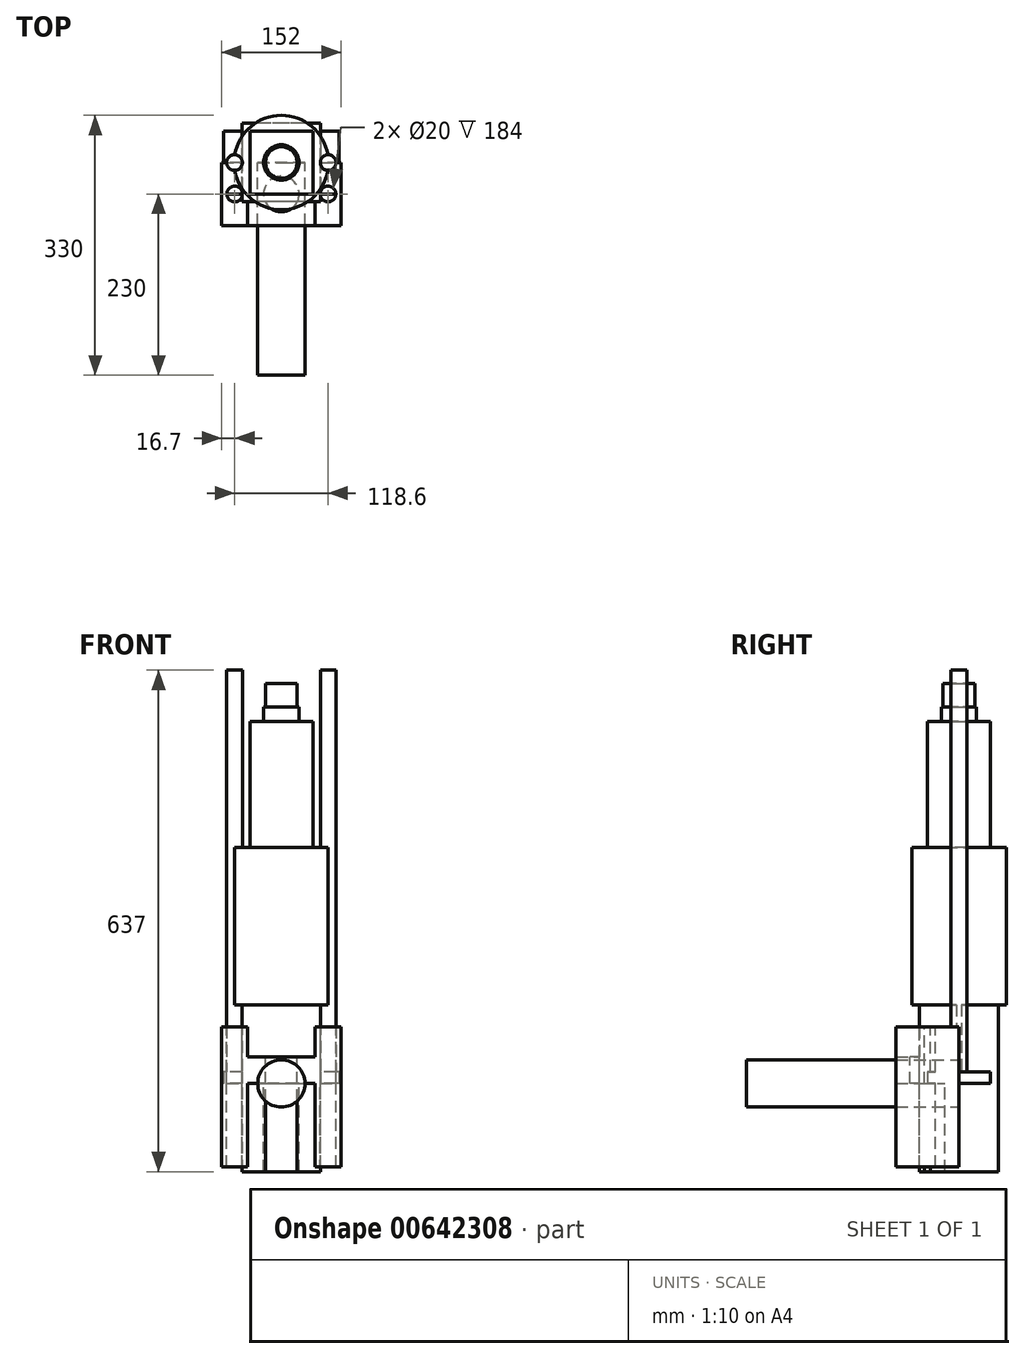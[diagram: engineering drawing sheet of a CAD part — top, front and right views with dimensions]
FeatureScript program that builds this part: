
annotation { "Feature Type Name" : "Feature", "Feature Type Description" : "" }
export const myFeature = defineFeature(function(context is Context, id is Id, definition is map)
    precondition{}
    {
        {
            var Q0;
            Q0=qCreatedBy(makeId("Top.planeOp"),FACE);
            var sketch = newSketch(context, id + "F0", { "sketchPlane" : qUnion([Q0])});
            skLineSegment(sketch, "E0.bottom", {"start": v(40, -40) * mm, "end": v(-40, -40) * mm});
            skLineSegment(sketch, "E0.top", {"start": v(40, 40) * mm, "end": v(-40, 40) * mm});
            skLineSegment(sketch, "E0.left", {"start": v(40, -40) * mm, "end": v(40, 40) * mm});
            skLineSegment(sketch, "E0.right", {"start": v(-40, -40) * mm, "end": v(-40, 40) * mm});
            skPoint(sketch, "E0.middle", {"position": v(0, 0) * mm});
            skSolve(sketch);
        }
        {
            var Q0;
            Q0=makeQuery(id+"F0.imprint","IMPRINT",FACE,{"disambiguationData":[TD([[makeQuery(id+"F0.imprint","IMPRINT",EDGE,{"derivedFrom":sQuery(id+"F0.wireOp",EDGE,"E0.bottom")}),-1.0]])]});
            extrude(context, id + "F1", {"entities" : qUnion([Q0]), "depth" : (620 - 112 - 48) * mm, "offsetDistance" : 25 * mm});
        }
        {
            var Q0;
            Q0=makeQuery(id+"F1.opExtrude","CAP_FACE",FACE,{"disambiguationData":[OSD([sQuery(id+"F0.wireOp",EDGE,"E0.bottom"),sQuery(id+"F0.wireOp",EDGE,"E0.top"),sQuery(id+"F0.wireOp",EDGE,"E0.left"),sQuery(id+"F0.wireOp",EDGE,"E0.right")])],"isStart":true});
            var sketch = newSketch(context, id + "F2", { "sketchPlane" : qUnion([Q0])});
            skLineSegment(sketch, "E1.bottom", {"start": v(50, -50) * mm, "end": v(-50, -50) * mm});
            skLineSegment(sketch, "E1.top", {"start": v(50, 50) * mm, "end": v(-50, 50) * mm});
            skLineSegment(sketch, "E1.left", {"start": v(50, -50) * mm, "end": v(50, 50) * mm});
            skLineSegment(sketch, "E1.right", {"start": v(-50, -50) * mm, "end": v(-50, 50) * mm});
            skPoint(sketch, "E1.middle", {"position": v(0, 0) * mm});
            skSolve(sketch);
        }
        {
            var Q0;
            Q0=makeQuery(id+"F2.imprint","IMPRINT",FACE,{"disambiguationData":[TD([[makeQuery(id+"F2.imprint","IMPRINT",EDGE,{"derivedFrom":makeQuery(id+"F1.opExtrude","CAP_EDGE",EDGE,{"disambiguationData":[OSD([sQuery(id+"F0.wireOp",EDGE,"E0.bottom")])],"isStart":true})}),1.0]])]});
            var Q1;
            Q1=makeQuery(id+"F2.imprint","IMPRINT",FACE,{"disambiguationData":[TD([[makeQuery(id+"F2.imprint","IMPRINT",EDGE,{"derivedFrom":sQuery(id+"F2.wireOp",EDGE,"E1.bottom")}),-1.0]])]});
            extrude(context, id + "F3", {"entities" : qUnion([Q0, Q1]), "operationType" : NewBodyOperationType.ADD, "depth" : 112 * mm, "offsetDistance" : 25 * mm});
        }
        {
            var Q0;
            Q0=makeQuery(id+"F1.opExtrude","CAP_FACE",FACE,{"disambiguationData":[OSD([sQuery(id+"F0.wireOp",EDGE,"E0.bottom"),sQuery(id+"F0.wireOp",EDGE,"E0.top"),sQuery(id+"F0.wireOp",EDGE,"E0.left"),sQuery(id+"F0.wireOp",EDGE,"E0.right")])],"isStart":false});
            var sketch = newSketch(context, id + "F4", { "sketchPlane" : qUnion([Q0])});
            skCircle(sketch, "E2", {"center": v(0, 0) * mm, "radius": 22.5 * mm});
            skCircle(sketch, "E3", {"center": v(0, 0) * mm, "radius": 20 * mm});
            skSolve(sketch);
        }
        {
            var Q0;
            Q0=makeQuery(id+"F4.imprint","IMPRINT",FACE,{"disambiguationData":[TD([[makeQuery(id+"F4.imprint","IMPRINT",EDGE,{"derivedFrom":sQuery(id+"F4.wireOp",EDGE,"E2")}),1.0]])]});
            extrude(context, id + "F5", {"entities" : qUnion([Q0]), "operationType" : NewBodyOperationType.ADD, "depth" : 18.5 * mm, "offsetDistance" : 25 * mm});
        }
        {
            var Q0;
            Q0=makeQuery(id+"F5.boolean.opBoolean","SPLIT",FACE,{"disambiguationData":[TD([makeQuery(id+"F5.opExtrude","SWEPT_FACE",FACE,{"disambiguationData":[OSD([sQuery(id+"F4.wireOp",EDGE,"E3")])]})])],"derivedFrom":makeQuery(id+"F1.opExtrude","CAP_FACE",FACE,{"disambiguationData":[OSD([sQuery(id+"F0.wireOp",EDGE,"E0.bottom"),sQuery(id+"F0.wireOp",EDGE,"E0.top"),sQuery(id+"F0.wireOp",EDGE,"E0.left"),sQuery(id+"F0.wireOp",EDGE,"E0.right")])],"isStart":false})});
            extrude(context, id + "F6", {"entities" : qUnion([Q0]), "operationType" : NewBodyOperationType.ADD, "depth" : 48 * mm, "offsetDistance" : 25 * mm});
        }
        {
            var Q0;
            Q0=qCreatedBy(makeId("Top.planeOp"),FACE);
            var sketch = newSketch(context, id + "F7", { "sketchPlane" : qUnion([Q0])});
            skCircle(sketch, "E4", {"center": v(0, 0) * mm, "radius": 20 * mm});
            skSolve(sketch);
        }
        {
            var Q0;
            Q0=makeQuery(id+"F7.imprint","IMPRINT",FACE,{"disambiguationData":[TD([[makeQuery(id+"F7.imprint","IMPRINT",EDGE,{"derivedFrom":sQuery(id+"F7.wireOp",EDGE,"E4")}),1.0]])]});
            extrude(context, id + "F8", {"entities" : qUnion([Q0]), "depth" : 400 * mm, "offsetDistance" : 25 * mm});
        }
        {
            var Q0;
            Q0=qCreatedBy(makeId("Front.planeOp"),FACE);
            var sketch = newSketch(context, id + "F9", { "sketchPlane" : qUnion([Q0])});
            skLineSegment(sketch, "E5", {"start": v(0, 0) * mm, "end": v(42.6, 0) * mm});
            skLineSegment(sketch, "E6", {"start": v(42.6, 0) * mm, "end": v(42.6, -106) * mm});
            skLineSegment(sketch, "E7", {"start": v(42.6, -106) * mm, "end": v(76, -106) * mm});
            skLineSegment(sketch, "E8", {"start": v(76, -106) * mm, "end": v(76, 72) * mm});
            skLineSegment(sketch, "E9", {"start": v(76, 72) * mm, "end": v(42.6, 72) * mm});
            skLineSegment(sketch, "E10", {"start": v(42.6, 72) * mm, "end": v(42.6, 34) * mm});
            skLineSegment(sketch, "E11", {"start": v(42.6, 34) * mm, "end": v(-42.6, 34) * mm});
            skLineSegment(sketch, "E12", {"start": v(-42.6, 34) * mm, "end": v(-42.6, 72) * mm});
            skLineSegment(sketch, "E13", {"start": v(-42.6, 72) * mm, "end": v(-76, 72) * mm});
            skLineSegment(sketch, "E14", {"start": v(-76, 72) * mm, "end": v(-76, -106) * mm});
            skLineSegment(sketch, "E15", {"start": v(-76, -106) * mm, "end": v(-42.6, -106) * mm});
            skLineSegment(sketch, "E16", {"start": v(-42.6, -106) * mm, "end": v(-42.6, 0) * mm});
            skLineSegment(sketch, "E17", {"start": v(-42.6, 0) * mm, "end": v(0, 0) * mm});
            skSolve(sketch);
        }
        {
            var Q0;
            Q0=makeQuery(id+"F9.imprint","IMPRINT",FACE,{"disambiguationData":[TD([[makeQuery(id+"F9.imprint","IMPRINT",EDGE,{"derivedFrom":sQuery(id+"F9.wireOp",EDGE,"E5")}),1.0]])]});
            extrude(context, id + "F10", {"entities" : qUnion([Q0]), "depth" : 80 * mm, "offsetDistance" : 25 * mm});
        }
        {
            var Q0;
            Q0=makeQuery(id+"F10.opExtrude","SWEPT_FACE",FACE,{"disambiguationData":[OSD([sQuery(id+"F9.wireOp",EDGE,"E13")])]});
            var sketch = newSketch(context, id + "F11", { "sketchPlane" : qUnion([Q0])});
            skCircle(sketch, "E18", {"center": v(-59.3, -40) * mm, "radius": 10 * mm});
            skPoint(sketch, "E18.centerSnap0", {"position": v(-59.3, -80) * mm});
            skSolve(sketch);
        }
        {
            var Q0;
            Q0=makeQuery(id+"F11.imprint","IMPRINT",FACE,{"disambiguationData":[TD([[makeQuery(id+"F11.imprint","IMPRINT",EDGE,{"derivedFrom":sQuery(id+"F11.wireOp",EDGE,"E18")}),1.0]])]});
            extrude(context, id + "F12", {"entities" : qUnion([Q0]), "operationType" : NewBodyOperationType.REMOVE, "endBound" : BoundingType.THROUGH_ALL, "oppositeDirection" : true, "depth" : 25 * mm, "offsetDistance" : 25 * mm});
        }
        {
            var Q0;
            Q0=makeQuery(id+"F10.opExtrude","SWEPT_FACE",FACE,{"disambiguationData":[OSD([sQuery(id+"F9.wireOp",EDGE,"E9")])]});
            var sketch = newSketch(context, id + "F13", { "sketchPlane" : qUnion([Q0])});
            skCircle(sketch, "E19", {"center": v(59.3, -40) * mm, "radius": 10 * mm});
            skPoint(sketch, "E19.centerSnap0", {"position": v(76, -40) * mm});
            skPoint(sketch, "E19.centerSnap1", {"position": v(59.3, -80) * mm});
            skSolve(sketch);
        }
        {
            var Q0;
            Q0=makeQuery(id+"F13.imprint","IMPRINT",FACE,{"disambiguationData":[TD([[makeQuery(id+"F13.imprint","IMPRINT",EDGE,{"derivedFrom":sQuery(id+"F13.wireOp",EDGE,"E19")}),1.0]])]});
            extrude(context, id + "F14", {"entities" : qUnion([Q0]), "operationType" : NewBodyOperationType.REMOVE, "endBound" : BoundingType.THROUGH_ALL, "oppositeDirection" : true, "depth" : 25 * mm, "offsetDistance" : 25 * mm});
        }
        {
            var Q0;
            Q0=makeQuery(id+"F10.opExtrude","SWEPT_FACE",FACE,{"disambiguationData":[OSD([sQuery(id+"F9.wireOp",EDGE,"E11")])]});
            var sketch = newSketch(context, id + "F15", { "sketchPlane" : qUnion([Q0])});
            skCircle(sketch, "E20", {"center": v(0, -40) * mm, "radius": 22.5 * mm});
            skPoint(sketch, "E20.centerSnap0", {"position": v(42.6, -40) * mm});
            skSolve(sketch);
        }
        {
            var Q0;
            Q0=makeQuery(id+"F15.imprint","IMPRINT",FACE,{"disambiguationData":[TD([[makeQuery(id+"F15.imprint","IMPRINT",EDGE,{"derivedFrom":sQuery(id+"F15.wireOp",EDGE,"E20")}),1.0]])]});
            extrude(context, id + "F16", {"entities" : qUnion([Q0]), "operationType" : NewBodyOperationType.REMOVE, "endBound" : BoundingType.THROUGH_ALL, "oppositeDirection" : true, "depth" : 25 * mm, "offsetDistance" : 25 * mm});
        }
        {
            var Q0;
            Q0=qCreatedBy(makeId("Top.planeOp"),FACE);
            var sketch = newSketch(context, id + "F17", { "sketchPlane" : qUnion([Q0])});
            skLineSegment(sketch, "E21.bottom", {"start": v(73.5, -40) * mm, "end": v(-73.5, -40) * mm});
            skLineSegment(sketch, "E21.top", {"start": v(73.5, 40) * mm, "end": v(-73.5, 40) * mm});
            skLineSegment(sketch, "E21.left", {"start": v(73.5, -40) * mm, "end": v(73.5, 40) * mm});
            skLineSegment(sketch, "E21.right", {"start": v(-73.5, -40) * mm, "end": v(-73.5, 40) * mm});
            skPoint(sketch, "E21.middle", {"position": v(0, 0) * mm});
            skSolve(sketch);
        }
        {
            var Q0;
            Q0=makeQuery(id+"F17.imprint","IMPRINT",FACE,{"disambiguationData":[TD([[makeQuery(id+"F17.imprint","IMPRINT",EDGE,{"derivedFrom":sQuery(id+"F17.wireOp",EDGE,"E21.bottom")}),-1.0]])]});
            extrude(context, id + "F18", {"entities" : qUnion([Q0]), "depth" : 15 * mm, "offsetDistance" : 25 * mm});
        }
        {
            var Q0;
            Q0=makeQuery(id+"F18.opExtrude","CAP_FACE",FACE,{"disambiguationData":[OSD([sQuery(id+"F17.wireOp",EDGE,"E21.bottom"),sQuery(id+"F17.wireOp",EDGE,"E21.top"),sQuery(id+"F17.wireOp",EDGE,"E21.left"),sQuery(id+"F17.wireOp",EDGE,"E21.right")])],"isStart":false});
            var sketch = newSketch(context, id + "F19", { "sketchPlane" : qUnion([Q0])});
            skCircle(sketch, "E22", {"center": v(-59.5, 0) * mm, "radius": 10 * mm});
            skCircle(sketch, "E23", {"center": v(59.5, 0) * mm, "radius": 10 * mm});
            skLineSegment(sketch, "E24", {"start": v(-73.5, 0) * mm, "end": v(-59.5, 0) * mm, "construction": true});
            skLineSegment(sketch, "E25", {"start": v(59.5, 0) * mm, "end": v(73.5, 0) * mm, "construction": true});
            skSolve(sketch);
        }
        {
            var Q0;
            Q0=makeQuery(id+"F19.imprint","IMPRINT",FACE,{"disambiguationData":[TD([[makeQuery(id+"F19.imprint","IMPRINT",EDGE,{"derivedFrom":sQuery(id+"F19.wireOp",EDGE,"E22")}),1.0]])]});
            var Q1;
            Q1=makeQuery(id+"F19.imprint","IMPRINT",FACE,{"disambiguationData":[TD([[makeQuery(id+"F19.imprint","IMPRINT",EDGE,{"derivedFrom":sQuery(id+"F19.wireOp",EDGE,"E23")}),1.0]])]});
            extrude(context, id + "F20", {"entities" : qUnion([Q0, Q1]), "operationType" : NewBodyOperationType.ADD, "depth" : (225 - 15 + 300) * mm, "offsetDistance" : 25 * mm});
        }
        {
            var Q0;
            Q0=qCreatedBy(makeId("Top.planeOp"),FACE);
            var sketch = newSketch(context, id + "F21", { "sketchPlane" : qUnion([Q0])});
            skLineSegment(sketch, "E26.bottom", {"start": v(50, -50) * mm, "end": v(-50, -50) * mm});
            skLineSegment(sketch, "E26.top", {"start": v(50, 50) * mm, "end": v(-50, 50) * mm});
            skLineSegment(sketch, "E26.left", {"start": v(50, -50) * mm, "end": v(50, 50) * mm});
            skLineSegment(sketch, "E26.right", {"start": v(-50, -50) * mm, "end": v(-50, 50) * mm});
            skPoint(sketch, "E26.middle", {"position": v(0, 0) * mm});
            skSolve(sketch);
        }
        {
            var Q0;
            Q0=makeQuery(id+"F21.imprint","IMPRINT",FACE,{"disambiguationData":[TD([[makeQuery(id+"F21.imprint","IMPRINT",EDGE,{"derivedFrom":sQuery(id+"F21.wireOp",EDGE,"E26.bottom")}),-1.0]])]});
            extrude(context, id + "F22", {"entities" : qUnion([Q0]), "depth" : 100 * mm, "offsetDistance" : 25 * mm});
        }
        {
            var Q0;
            Q0=qCreatedBy(makeId("Front.planeOp"),FACE);
            var sketch = newSketch(context, id + "F23", { "sketchPlane" : qUnion([Q0])});
            skCircle(sketch, "E27", {"center": v(0, 0) * mm, "radius": 30 * mm});
            skSolve(sketch);
        }
        {
            var Q0;
            Q0=makeQuery(id+"F23.imprint","IMPRINT",FACE,{"disambiguationData":[TD([[makeQuery(id+"F23.imprint","IMPRINT",EDGE,{"derivedFrom":sQuery(id+"F23.wireOp",EDGE,"E27")}),1.0]])]});
            extrude(context, id + "F24", {"entities" : qUnion([Q0]), "depth" : (540 / 2) * mm, "offsetDistance" : 25 * mm});
        }
        {
            var Q0;
            Q0=makeQuery(id+"F22.opExtrude","CAP_FACE",FACE,{"disambiguationData":[OSD([sQuery(id+"F21.wireOp",EDGE,"E26.bottom"),sQuery(id+"F21.wireOp",EDGE,"E26.top"),sQuery(id+"F21.wireOp",EDGE,"E26.left"),sQuery(id+"F21.wireOp",EDGE,"E26.right")])],"isStart":false});
            var sketch = newSketch(context, id + "F25", { "sketchPlane" : qUnion([Q0])});
            skCircle(sketch, "E28", {"center": v(0, 0) * mm, "radius": 60 * mm});
            skSolve(sketch);
        }
        {
            var Q0;
            {var subQ0=sQuery(id+"F25.wireOp",EDGE,"E28");var subQ8=makeQuery(id+"F22.opExtrude","CAP_EDGE",EDGE,{"disambiguationData":[OSD([sQuery(id+"F21.wireOp",EDGE,"E26.top")])],"isStart":false});var subQ11=makeQuery(id+"F25.imprint","INTERSECT",VERTEX,{"disambiguationData":[OD(0.0)],"derivedFrom":[subQ8,subQ0]});Q0=makeQuery(id+"F25.imprint","IMPRINT",FACE,{"disambiguationData":[TD([[makeQuery(id+"F25.imprint","IMPRINT",EDGE,{"disambiguationData":[TD([[subQ11,1.0]])],"derivedFrom":subQ0}),1.0]])]});}
            var Q1;
            {var subQ0=sQuery(id+"F25.wireOp",EDGE,"E28");var subQ1=makeQuery(id+"F22.opExtrude","CAP_EDGE",EDGE,{"disambiguationData":[OSD([sQuery(id+"F21.wireOp",EDGE,"E26.right")])],"isStart":false});var subQ2=makeQuery(id+"F25.imprint","INTERSECT",VERTEX,{"disambiguationData":[OD(0.0)],"derivedFrom":[subQ1,subQ0]});Q1=makeQuery(id+"F25.imprint","IMPRINT",FACE,{"disambiguationData":[TD([[makeQuery(id+"F25.imprint","IMPRINT",EDGE,{"disambiguationData":[TD([[subQ2,-1.0]])],"derivedFrom":subQ0}),1.0]])]});}
            var Q2;
            {var subQ0=sQuery(id+"F25.wireOp",EDGE,"E28");var subQ1=makeQuery(id+"F22.opExtrude","CAP_EDGE",EDGE,{"disambiguationData":[OSD([sQuery(id+"F21.wireOp",EDGE,"E26.bottom")])],"isStart":false});var subQ2=makeQuery(id+"F25.imprint","INTERSECT",VERTEX,{"disambiguationData":[OD(0.0)],"derivedFrom":[subQ1,subQ0]});Q2=makeQuery(id+"F25.imprint","IMPRINT",FACE,{"disambiguationData":[TD([[makeQuery(id+"F25.imprint","IMPRINT",EDGE,{"disambiguationData":[TD([[subQ2,-1.0]])],"derivedFrom":subQ0}),1.0]])]});}
            var Q3;
            {var subQ0=sQuery(id+"F25.wireOp",EDGE,"E28");var subQ1=makeQuery(id+"F22.opExtrude","CAP_EDGE",EDGE,{"disambiguationData":[OSD([sQuery(id+"F21.wireOp",EDGE,"E26.left")])],"isStart":false});var subQ2=makeQuery(id+"F25.imprint","INTERSECT",VERTEX,{"disambiguationData":[OD(0.0)],"derivedFrom":[subQ1,subQ0]});Q3=makeQuery(id+"F25.imprint","IMPRINT",FACE,{"disambiguationData":[TD([[makeQuery(id+"F25.imprint","IMPRINT",EDGE,{"disambiguationData":[TD([[subQ2,1.0]])],"derivedFrom":subQ0}),1.0]])]});}
            var Q4;
            {var subQ0=sQuery(id+"F25.wireOp",EDGE,"E28");var subQ1=makeQuery(id+"F22.opExtrude","CAP_EDGE",EDGE,{"disambiguationData":[OSD([sQuery(id+"F21.wireOp",EDGE,"E26.top")])],"isStart":false});var subQ2=makeQuery(id+"F25.imprint","INTERSECT",VERTEX,{"disambiguationData":[OD(0.0)],"derivedFrom":[subQ1,subQ0]});Q4=makeQuery(id+"F25.imprint","IMPRINT",FACE,{"disambiguationData":[TD([[makeQuery(id+"F25.imprint","IMPRINT",EDGE,{"disambiguationData":[TD([[subQ2,-1.0]])],"derivedFrom":subQ0}),1.0]])]});}
            extrude(context, id + "F26", {"entities" : qUnion([Q0, Q1, Q2, Q3, Q4]), "operationType" : NewBodyOperationType.ADD, "depth" : 200 * mm, "offsetDistance" : 25 * mm});
        }
    });
